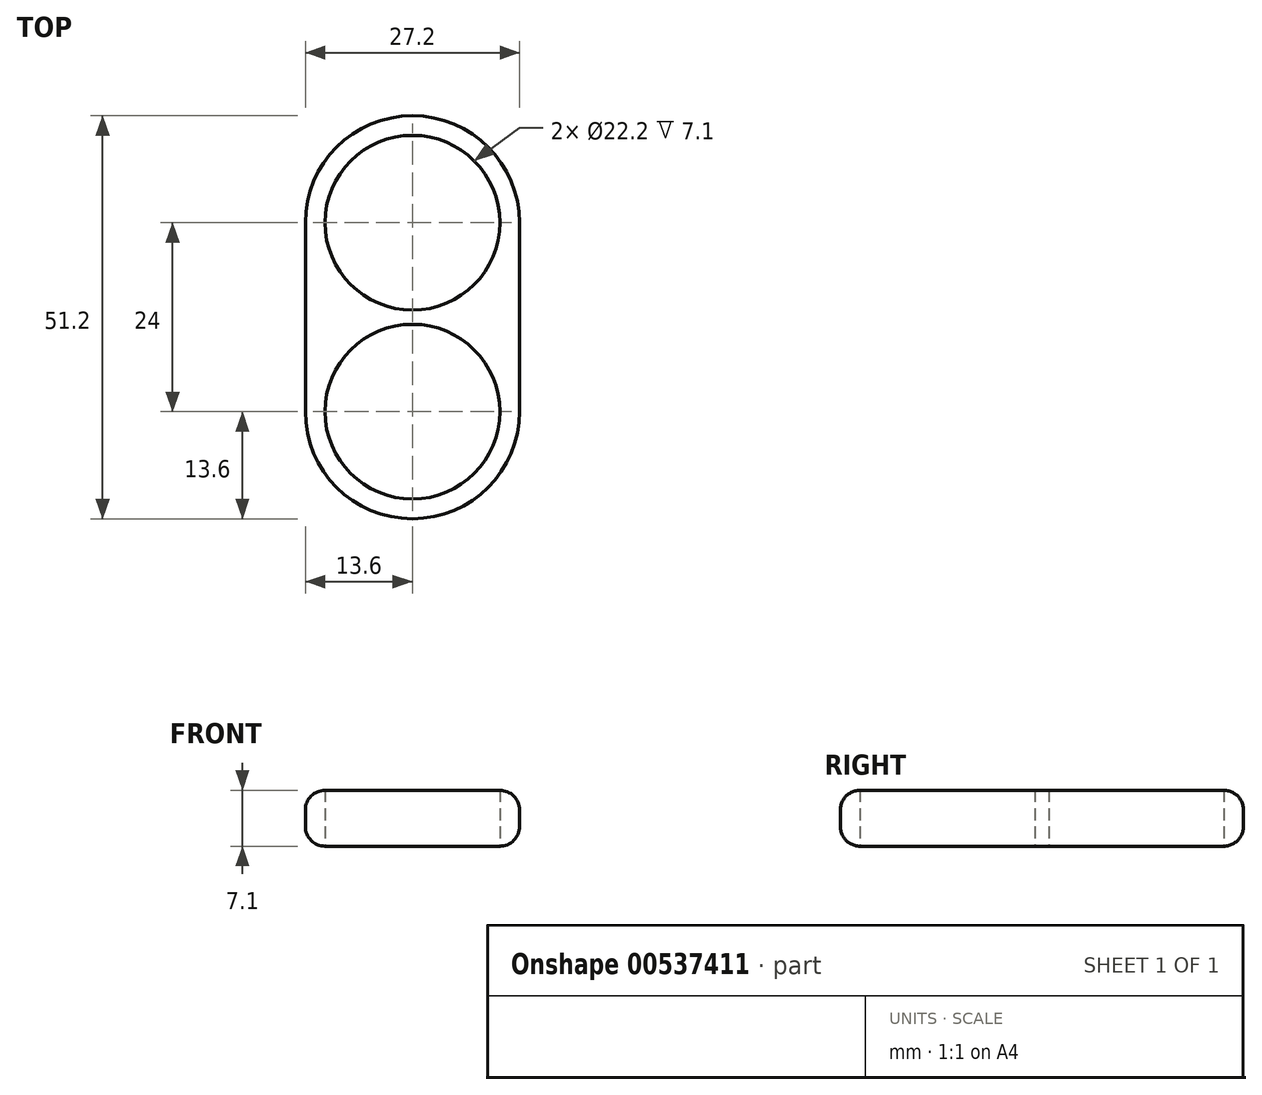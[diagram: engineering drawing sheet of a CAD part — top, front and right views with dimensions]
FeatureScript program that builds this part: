
annotation { "Feature Type Name" : "Feature", "Feature Type Description" : "" }
export const myFeature = defineFeature(function(context is Context, id is Id, definition is map)
    precondition{}
    {
        {
            var Q0;
            Q0=qCreatedBy(makeId("Top.planeOp"),FACE);
            var sketch = newSketch(context, id + "F0", { "sketchPlane" : qUnion([Q0])});
            skCircle(sketch, "E0", {"center": v(0, 0) * mm, "radius": 11.1 * mm});
            skLineSegment(sketch, "E1", {"start": v(0, 0) * mm, "end": v(0, 24) * mm});
            skCircle(sketch, "E2", {"center": v(0, 24) * mm, "radius": 11.1 * mm});
            skCircle(sketch, "E3.0", {"center": v(0, 24) * mm, "radius": 13.6 * mm});
            skCircle(sketch, "E4.0", {"center": v(0, 0) * mm, "radius": 13.6 * mm});
            skLineSegment(sketch, "E5", {"start": v(13.6, 24) * mm, "end": v(13.6, 0) * mm});
            skLineSegment(sketch, "E6", {"start": v(-13.6, 24) * mm, "end": v(-13.6, 0) * mm});
            skSolve(sketch);
        }
        {
            var Q0;
            {var subQ0=sQuery(id+"F0.wireOp",EDGE,"E6");Q0=makeQuery(id+"F0.imprint","IMPRINT",FACE,{"disambiguationData":[TD([[makeQuery(id+"F0.imprint","IMPRINT",EDGE,{"derivedFrom":subQ0}),1.0]])]});}
            var Q1;
            {var subQ0=sQuery(id+"F0.wireOp",EDGE,"E5");Q1=makeQuery(id+"F0.imprint","IMPRINT",FACE,{"disambiguationData":[TD([[makeQuery(id+"F0.imprint","IMPRINT",EDGE,{"derivedFrom":subQ0}),-1.0]])]});}
            var Q2;
            {var subQ0=sQuery(id+"F0.wireOp",EDGE,"E3.0");var subQ1=sQuery(id+"F0.wireOp",EDGE,"E0");var subQ2=makeQuery(id+"F0.imprint","INTERSECT",VERTEX,{"disambiguationData":[OD(0.0)],"derivedFrom":[subQ1,subQ0]});Q2=makeQuery(id+"F0.imprint","IMPRINT",FACE,{"disambiguationData":[TD([[makeQuery(id+"F0.imprint","IMPRINT",EDGE,{"disambiguationData":[TD([[subQ2,1.0]])],"derivedFrom":subQ1}),-1.0]])]});}
            var Q3;
            {var subQ0=sQuery(id+"F0.wireOp",EDGE,"E1");var subQ1=sQuery(id+"F0.wireOp",EDGE,"E0");var subQ2=makeQuery(id+"F0.imprint","INTERSECT",VERTEX,{"derivedFrom":[subQ1,subQ0]});Q3=makeQuery(id+"F0.imprint","IMPRINT",FACE,{"disambiguationData":[TD([[makeQuery(id+"F0.imprint","IMPRINT",EDGE,{"disambiguationData":[TD([[subQ2,-1.0]])],"derivedFrom":subQ1}),-1.0]])]});}
            var Q4;
            {var subQ1=sQuery(id+"F0.wireOp",EDGE,"E1");var subQ6=sQuery(id+"F0.wireOp",EDGE,"E0");var subQ9=makeQuery(id+"F0.imprint","INTERSECT",VERTEX,{"derivedFrom":[subQ6,subQ1]});Q4=makeQuery(id+"F0.imprint","IMPRINT",FACE,{"disambiguationData":[TD([[makeQuery(id+"F0.imprint","IMPRINT",EDGE,{"disambiguationData":[TD([[subQ9,1.0]])],"derivedFrom":subQ6}),-1.0]])]});}
            var Q5;
            {var subQ2=sQuery(id+"F0.wireOp",EDGE,"E4.0");var subQ6=sQuery(id+"F0.wireOp",EDGE,"E2");var subQ7=makeQuery(id+"F0.imprint","INTERSECT",VERTEX,{"disambiguationData":[OD(0.0)],"derivedFrom":[subQ6,subQ2]});Q5=makeQuery(id+"F0.imprint","IMPRINT",FACE,{"disambiguationData":[TD([[makeQuery(id+"F0.imprint","IMPRINT",EDGE,{"disambiguationData":[TD([[subQ7,1.0]])],"derivedFrom":subQ6}),-1.0]])]});}
            extrude(context, id + "F1", {"entities" : qUnion([Q0, Q1, Q2, Q3, Q4, Q5]), "depth" : 7.1 * mm, "offsetDistance" : 25 * mm});
        }
        {
            var Q0;
            Q0=makeQuery(id+"F1.opExtrude","CAP_EDGE",EDGE,{"disambiguationData":[OSD([sQuery(id+"F0.wireOp",EDGE,"E5")])],"isStart":false});
            var Q1;
            Q1=makeQuery(id+"F1.opExtrude","CAP_EDGE",EDGE,{"disambiguationData":[OSD([sQuery(id+"F0.wireOp",EDGE,"E5")])],"isStart":true});
            fillet(context, id + "F2", {"entities" : qUnion([Q0, Q1]), "radius" : 2.5 * mm, "tangentPropagation" : true, "allowEdgeOverflow" : false});
        }
    });
